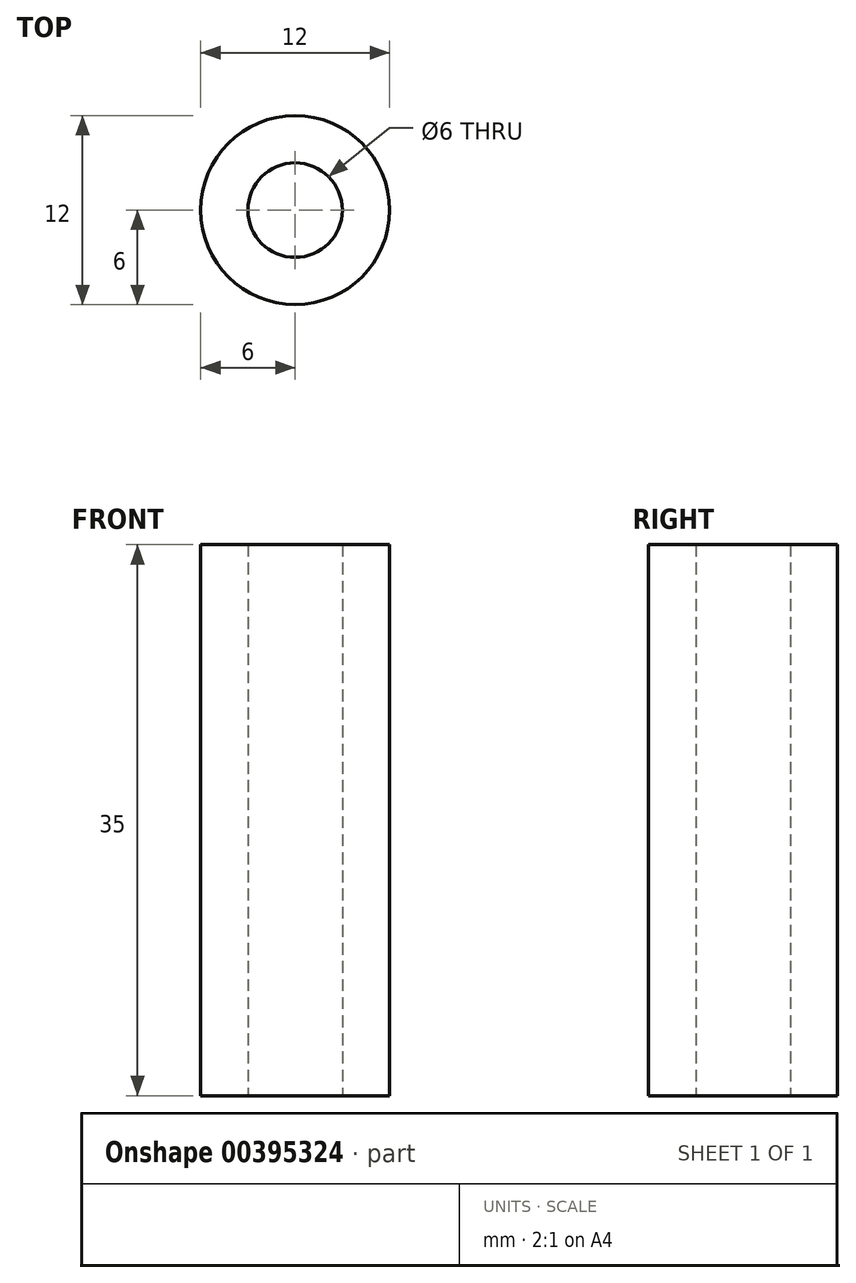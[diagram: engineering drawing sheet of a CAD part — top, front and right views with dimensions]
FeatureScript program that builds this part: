
annotation { "Feature Type Name" : "Feature", "Feature Type Description" : "" }
export const myFeature = defineFeature(function(context is Context, id is Id, definition is map)
    precondition{}
    {
        {
            var Q0;
            Q0=qCreatedBy(makeId("Top.planeOp"),FACE);
            var sketch = newSketch(context, id + "F0", { "sketchPlane" : qUnion([Q0])});
            skCircle(sketch, "E0", {"center": v(0, 0) * mm, "radius": 6 * mm});
            skCircle(sketch, "E1", {"center": v(0, 0) * mm, "radius": 3 * mm});
            skSolve(sketch);
        }
        {
            var Q0;
            Q0 = qSketchRegion(id + "F0", true);
            extrude(context, id + "F1", {"entities" : qUnion([Q0]), "depth" : 35 * mm});
        }
    });
